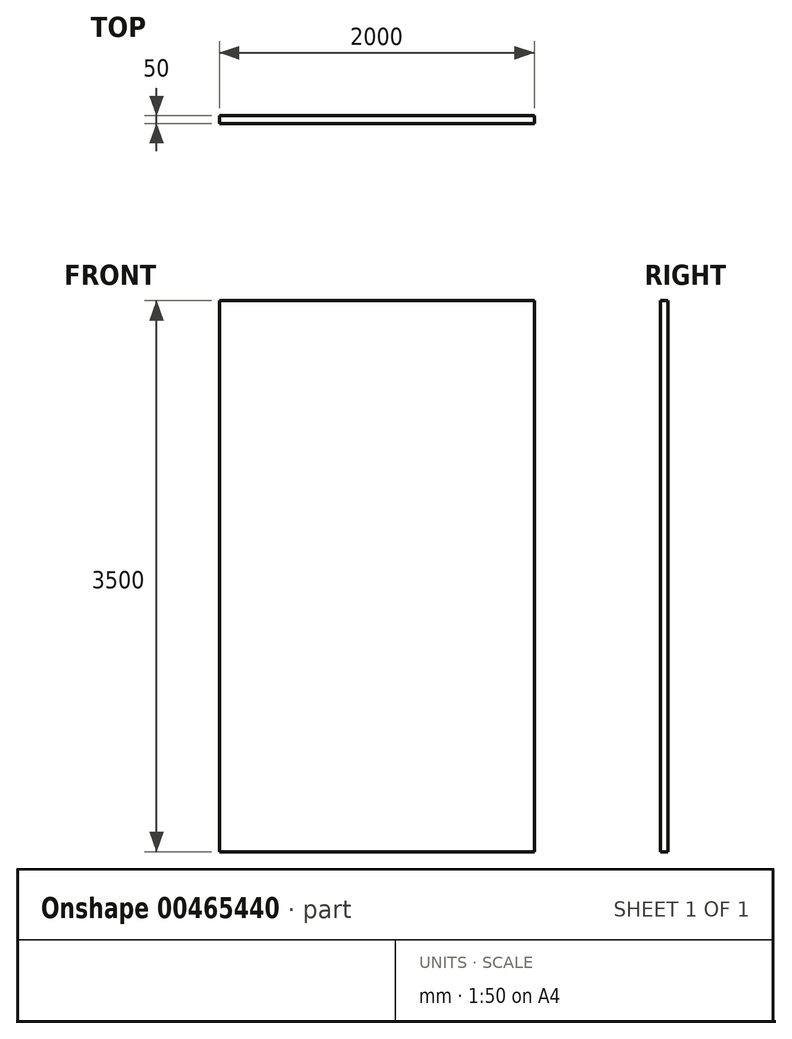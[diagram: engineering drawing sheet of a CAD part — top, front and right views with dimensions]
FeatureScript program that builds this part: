
annotation { "Feature Type Name" : "Feature", "Feature Type Description" : "" }
export const myFeature = defineFeature(function(context is Context, id is Id, definition is map)
    precondition{}
    {
        {
            var Q0;
            Q0=qCreatedBy(makeId("Top.planeOp"),FACE);
            var sketch = newSketch(context, id + "F0", { "sketchPlane" : qUnion([Q0])});
            skLineSegment(sketch, "E0.bottom", {"start": v(0, 0) * mm, "end": v(2000, 0) * mm});
            skLineSegment(sketch, "E0.top", {"start": v(0, 50) * mm, "end": v(2000, 50) * mm});
            skLineSegment(sketch, "E0.left", {"start": v(0, 0) * mm, "end": v(0, 50) * mm});
            skLineSegment(sketch, "E0.right", {"start": v(2000, 0) * mm, "end": v(2000, 50) * mm});
            skSolve(sketch);
        }
        {
            var Q0;
            Q0=makeQuery(id+"F0.imprint","IMPRINT",FACE,{"disambiguationData":[TD([[makeQuery(id+"F0.imprint","IMPRINT",EDGE,{"derivedFrom":sQuery(id+"F0.wireOp",EDGE,"E0.bottom")}),1.0]])]});
            extrude(context, id + "F1", {"entities" : qUnion([Q0]), "depth" : 3500 * mm});
        }
    });
